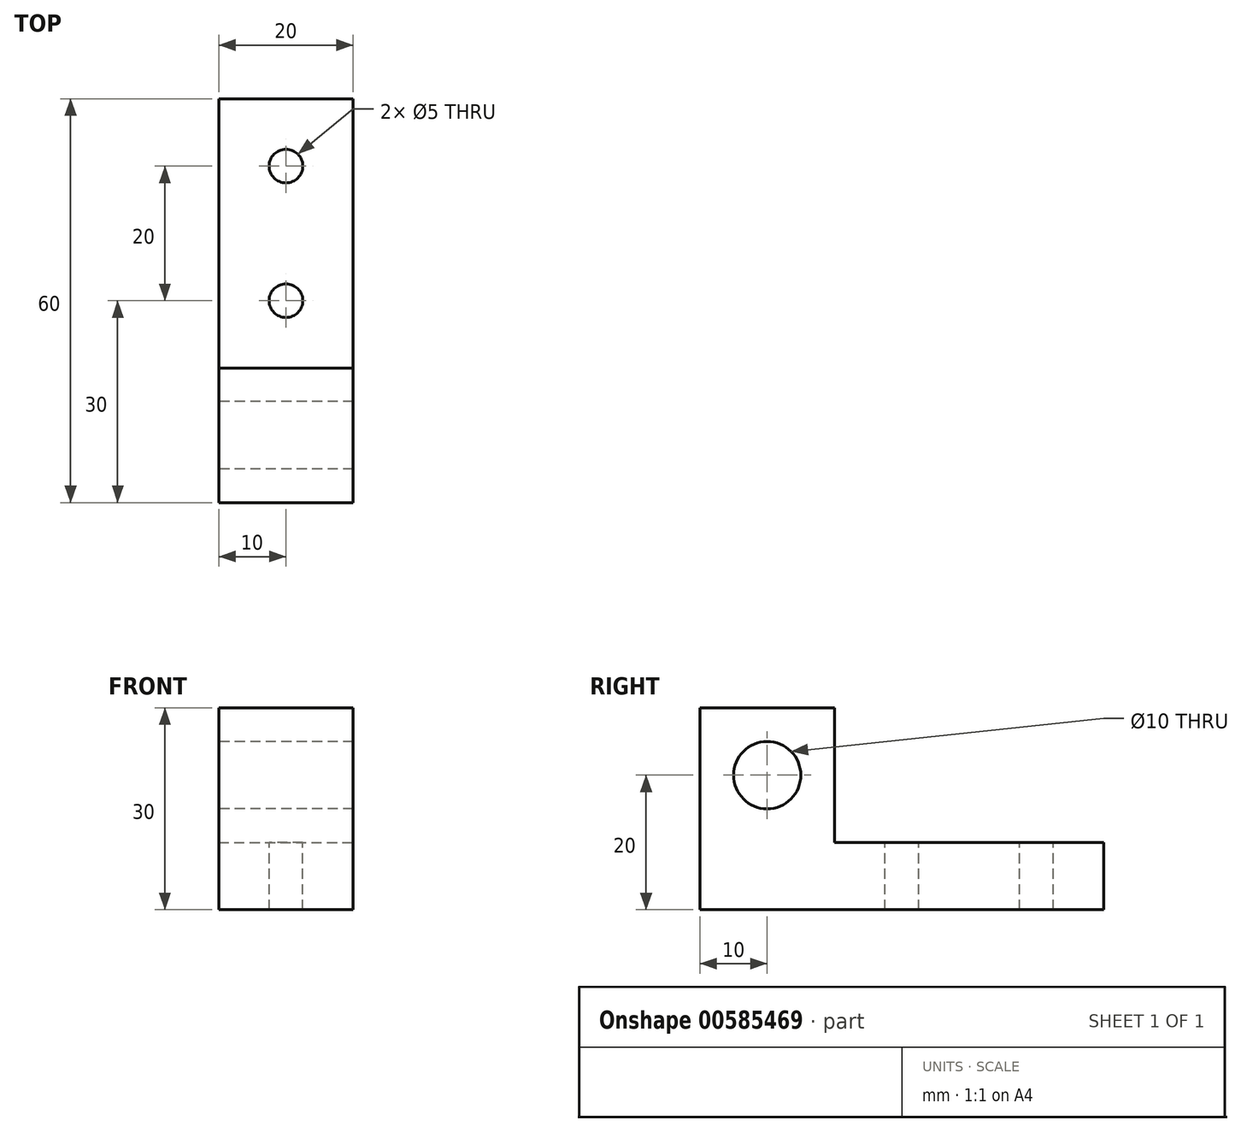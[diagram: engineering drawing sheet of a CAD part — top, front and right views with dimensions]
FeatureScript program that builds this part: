
annotation { "Feature Type Name" : "Feature", "Feature Type Description" : "" }
export const myFeature = defineFeature(function(context is Context, id is Id, definition is map)
    precondition{}
    {
        {
            var Q0;
            Q0=qCreatedBy(makeId("Top.planeOp"),FACE);
            var sketch = newSketch(context, id + "F0", { "sketchPlane" : qUnion([Q0])});
            skLineSegment(sketch, "E0.bottom", {"start": v(10, -30) * mm, "end": v(-10, -30) * mm});
            skLineSegment(sketch, "E0.top", {"start": v(10, 30) * mm, "end": v(-10, 30) * mm});
            skLineSegment(sketch, "E0.left", {"start": v(10, -30) * mm, "end": v(10, 30) * mm});
            skLineSegment(sketch, "E0.right", {"start": v(-10, -30) * mm, "end": v(-10, 30) * mm});
            skPoint(sketch, "E0.middle", {"position": v(0, 0) * mm});
            skSolve(sketch);
        }
        {
            var Q0;
            Q0 = qSketchRegion(id + "F0", true);
            extrude(context, id + "F1", {"entities" : qUnion([Q0]), "depth" : 10 * mm, "offsetDistance" : 25 * mm});
        }
        {
            var Q0;
            Q0=makeQuery(id+"F1.opExtrude","CAP_FACE",FACE,{"disambiguationData":[OSD([sQuery(id+"F0.wireOp",EDGE,"E0.bottom"),sQuery(id+"F0.wireOp",EDGE,"E0.top"),sQuery(id+"F0.wireOp",EDGE,"E0.left"),sQuery(id+"F0.wireOp",EDGE,"E0.right")])],"isStart":false});
            var sketch = newSketch(context, id + "F2", { "sketchPlane" : qUnion([Q0])});
            skLineSegment(sketch, "E1", {"start": v(-10, -10) * mm, "end": v(10, -10) * mm});
            skLineSegment(sketch, "E2", {"start": v(-10, -10) * mm, "end": v(-10, -30) * mm});
            skLineSegment(sketch, "E3", {"start": v(-10, -30) * mm, "end": v(10, -30) * mm});
            skLineSegment(sketch, "E4", {"start": v(10, -30) * mm, "end": v(10, -10) * mm});
            skSolve(sketch);
        }
        {
            var Q0;
            Q0=makeQuery(id+"F2.imprint","IMPRINT",FACE,{"disambiguationData":[TD([[makeQuery(id+"F2.imprint","IMPRINT",EDGE,{"derivedFrom":sQuery(id+"F2.wireOp",EDGE,"E1")}),-1.0]])]});
            extrude(context, id + "F3", {"entities" : qUnion([Q0]), "operationType" : NewBodyOperationType.ADD, "depth" : 20 * mm, "offsetDistance" : 25 * mm});
        }
        {
            var Q0;
            Q0=makeQuery(id+"F1.opExtrude","CAP_FACE",FACE,{"disambiguationData":[OSD([sQuery(id+"F0.wireOp",EDGE,"E0.bottom"),sQuery(id+"F0.wireOp",EDGE,"E0.top"),sQuery(id+"F0.wireOp",EDGE,"E0.left"),sQuery(id+"F0.wireOp",EDGE,"E0.right")])],"isStart":false});
            var sketch = newSketch(context, id + "F4", { "sketchPlane" : qUnion([Q0])});
            skLineSegment(sketch, "E5", {"start": v(0, 30) * mm, "end": v(0, 1.46) * mm, "construction": true});
            skPoint(sketch, "E6", {"position": v(0, 20) * mm});
            skSolve(sketch);
        }
        {
            var Q0;
            Q0=sQuery(id+"F4.wireOp",VERTEX,"E6");
            var Q1;
            Q1=makeQuery(id+"F1.opExtrude","SWEPT_BODY",BODY,{"disambiguationData":[OSD([sQuery(id+"F0.wireOp",EDGE,"E0.bottom"),sQuery(id+"F0.wireOp",EDGE,"E0.top"),sQuery(id+"F0.wireOp",EDGE,"E0.left"),sQuery(id+"F0.wireOp",EDGE,"E0.right")])]});
            hole(context, id + "F5", {"style" : HoleStyle.SIMPLE, "endStyle" : HoleEndStyle.THROUGH, "holeDiameter" : 5 * mm, "majorDiameter" : 5 * mm, "isTappedThrough" : true, "tappedDepth" : 12 * mm, "tapClearance" : 3, "locations" : qUnion([Q0]), "scope" : qUnion([Q1])});
        }
        {
            var Q0;
            Q0=makeQuery(id+"F1.opExtrude","CAP_FACE",FACE,{"disambiguationData":[OSD([sQuery(id+"F0.wireOp",EDGE,"E0.bottom"),sQuery(id+"F0.wireOp",EDGE,"E0.top"),sQuery(id+"F0.wireOp",EDGE,"E0.left"),sQuery(id+"F0.wireOp",EDGE,"E0.right")])],"isStart":false});
            var sketch = newSketch(context, id + "F6", { "sketchPlane" : qUnion([Q0])});
            skLineSegment(sketch, "E7", {"start": v(0, 30) * mm, "end": v(0, 4.91) * mm});
            skPoint(sketch, "E7.endSnap0", {"position": v(0, 30) * mm});
            skPoint(sketch, "E8", {"position": v(0, 0) * mm});
            skSolve(sketch);
        }
        {
            var Q0;
            Q0=sQuery(id+"F6.wireOp",VERTEX,"E8");
            var Q1;
            Q1=makeQuery(id+"F1.opExtrude","SWEPT_BODY",BODY,{"disambiguationData":[OSD([sQuery(id+"F0.wireOp",EDGE,"E0.bottom"),sQuery(id+"F0.wireOp",EDGE,"E0.top"),sQuery(id+"F0.wireOp",EDGE,"E0.left"),sQuery(id+"F0.wireOp",EDGE,"E0.right")])]});
            hole(context, id + "F7", {"style" : HoleStyle.SIMPLE, "endStyle" : HoleEndStyle.THROUGH, "holeDiameter" : 5 * mm, "majorDiameter" : 5 * mm, "isTappedThrough" : true, "tappedDepth" : 12 * mm, "tapClearance" : 3, "locations" : qUnion([Q0]), "scope" : qUnion([Q1])});
        }
        {
            var Q0;
            Q0=makeQuery(id+"F3.boolean.opBoolean","MERGE",FACE,{"derivedFrom":[makeQuery(id+"F1.opExtrude","SWEPT_FACE",FACE,{"disambiguationData":[OSD([sQuery(id+"F0.wireOp",EDGE,"E0.right")])]}),makeQuery(id+"F3.opExtrude","SWEPT_FACE",FACE,{"disambiguationData":[OSD([sQuery(id+"F2.wireOp",EDGE,"E2")])]})]});
            var sketch = newSketch(context, id + "F8", { "sketchPlane" : qUnion([Q0])});
            skLineSegment(sketch, "E9", {"start": v(10, 20) * mm, "end": v(30, 20) * mm, "construction": true});
            skPoint(sketch, "E10", {"position": v(20, 20) * mm});
            skSolve(sketch);
        }
        {
            var Q0;
            Q0=sQuery(id+"F8.wireOp",VERTEX,"E10");
            var Q1;
            Q1=makeQuery(id+"F1.opExtrude","SWEPT_BODY",BODY,{"disambiguationData":[OSD([sQuery(id+"F0.wireOp",EDGE,"E0.bottom"),sQuery(id+"F0.wireOp",EDGE,"E0.top"),sQuery(id+"F0.wireOp",EDGE,"E0.left"),sQuery(id+"F0.wireOp",EDGE,"E0.right")])]});
            hole(context, id + "F9", {"style" : HoleStyle.SIMPLE, "endStyle" : HoleEndStyle.THROUGH, "holeDiameter" : 10 * mm, "majorDiameter" : 5 * mm, "isTappedThrough" : true, "tappedDepth" : 12 * mm, "tapClearance" : 3, "locations" : qUnion([Q0]), "scope" : qUnion([Q1])});
        }
    });
